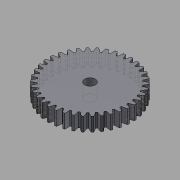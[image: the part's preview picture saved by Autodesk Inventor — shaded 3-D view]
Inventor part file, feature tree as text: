
AUTODESK INVENTOR PART (.ipt)
format: ipt  version: 2015 (Build 190159000, 159)  size: 290,304 bytes
history: native  units: mm (DEFAULTED — no unit token found)
features: plane x3, other x3, sketch x3, extrude x2
ambient origin geometry x8: Origin, YZ Plane, XZ Plane, XY Plane, X Axis, Y Axis, Z Axis, Center Point
bodies: Solid1 (feature_tree)
feature tree (11):
  extrude  "Extrusion1"  Depth=3.3mm TaperAngle=0.0deg
  plane  "Work Plane2"
  plane  "Work Plane8"
  plane  "Work Plane9"
  other  "Spur Gear"
  extrude  "Extrusion2"  Depth=10.0mm TaperAngle=0.0deg
  sketch  "Sketch1"  dims[d0=20.0mm d1=3.3mm d2=0.0mm]
  sketch  "Sketch2"  dims[d3=19.0mm d4=10.0mm d5=0.0mm]
  other  "Srf1"
  sketch  "Sketch3"  dims[d16=12.0mm d17=0.0mm d34=0.826735mm d39=0.0mm d41=0.0mm d43=12.0mm d46=12.0mm d47=0.0mm d48=0.0mm d49=2.5mm d50=10.0mm d51=0.0mm]
  other  "Pitch Diameter"
